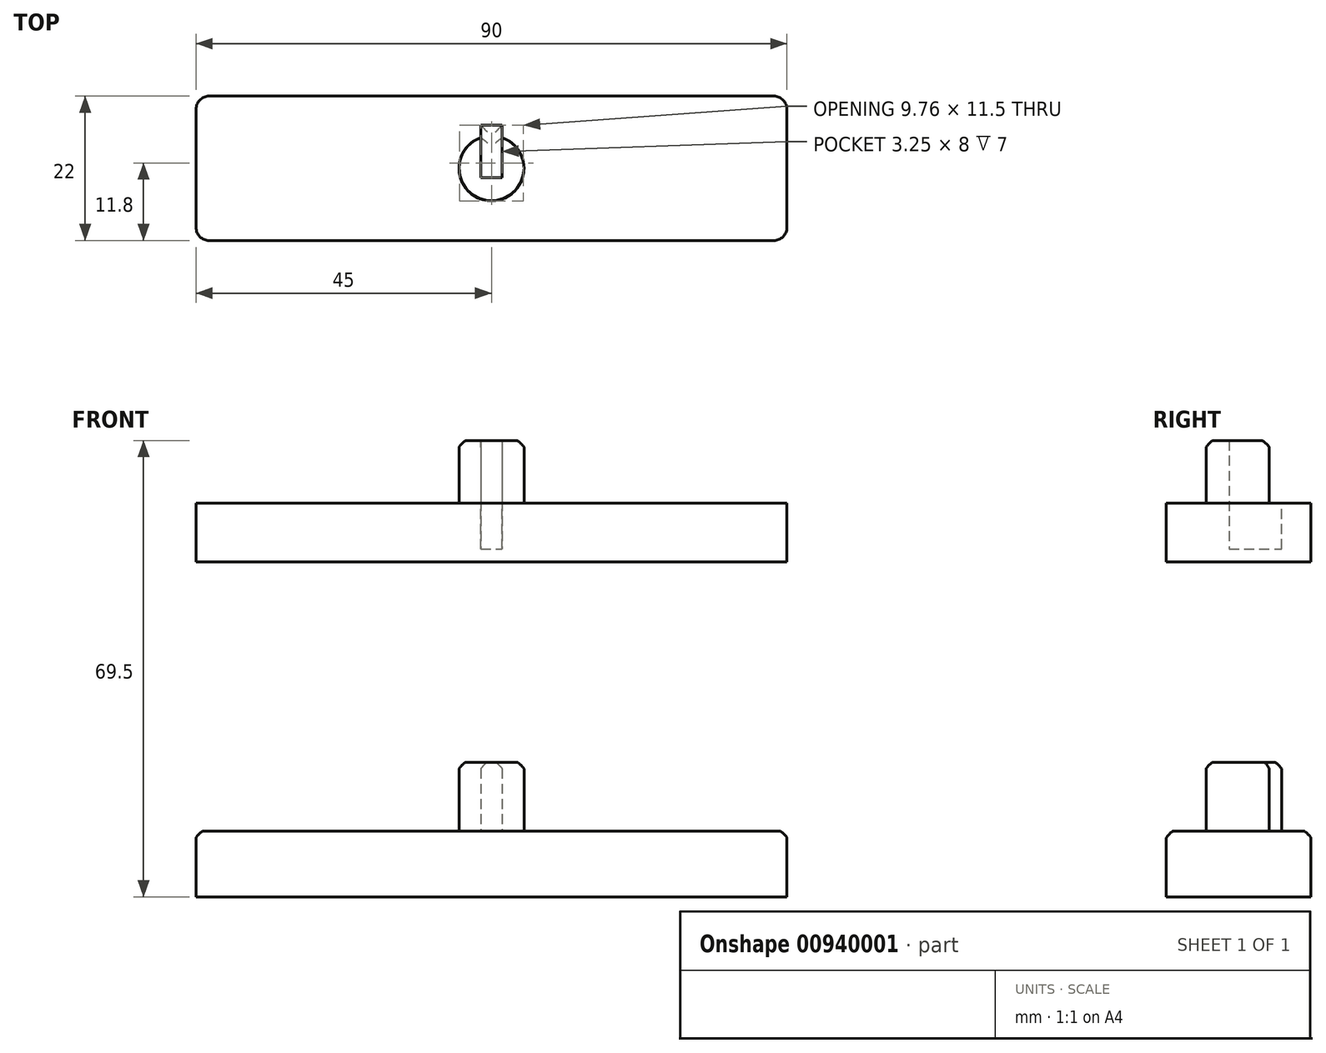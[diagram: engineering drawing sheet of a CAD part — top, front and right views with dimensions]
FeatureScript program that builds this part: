
annotation { "Feature Type Name" : "Feature", "Feature Type Description" : "" }
export const myFeature = defineFeature(function(context is Context, id is Id, definition is map)
    precondition{}
    {
        {
            var Q0;
            Q0=qCreatedBy(makeId("Top.planeOp"),FACE);
            var sketch = newSketch(context, id + "F0", { "sketchPlane" : qUnion([Q0])});
            skLineSegment(sketch, "E0.bottom", {"start": v(-43, 11) * mm, "end": v(43, 11) * mm});
            skLineSegment(sketch, "E0.top", {"start": v(-43, -11) * mm, "end": v(43, -11) * mm});
            skLineSegment(sketch, "E0.left", {"start": v(-45, 9) * mm, "end": v(-45, -9) * mm});
            skLineSegment(sketch, "E0.right", {"start": v(45, 9) * mm, "end": v(45, -9) * mm});
            skPoint(sketch, "E0.middle", {"position": v(0, 0) * mm});
            skArc(sketch, "E1", {"start": v(-1.62, 4.68) * mm, "mid": v(0, -4.95) * mm, "end": v(1.63, 4.68) * mm});
            skLineSegment(sketch, "E2", {"start": v(-1.62, 4.68) * mm, "end": v(-1.62, 6.55) * mm});
            skLineSegment(sketch, "E3", {"start": v(-1.62, 6.55) * mm, "end": v(0, 6.55) * mm});
            skLineSegment(sketch, "E4.MirrorCS", {"start": v(1.62, 4.68) * mm, "end": v(1.62, 6.55) * mm});
            skLineSegment(sketch, "E5.MirrorCS", {"start": v(1.62, 6.55) * mm, "end": v(0, 6.55) * mm});
            skPoint(sketch, "E6.visualSharp", {"position": v(-45, 11) * mm});
            skArc(sketch, "E6.filletArc", {"start": v(-43, 11) * mm, "mid": v(-44.41, 10.41) * mm, "end": v(-45, 9) * mm});
            skPoint(sketch, "E7.visualSharp", {"position": v(-45, -11) * mm});
            skArc(sketch, "E7.filletArc", {"start": v(-45, -9) * mm, "mid": v(-44.41, -10.41) * mm, "end": v(-43, -11) * mm});
            skPoint(sketch, "E8.visualSharp", {"position": v(45, -11) * mm});
            skArc(sketch, "E8.filletArc", {"start": v(43, -11) * mm, "mid": v(44.41, -10.41) * mm, "end": v(45, -9) * mm});
            skPoint(sketch, "E9.visualSharp", {"position": v(45, 11) * mm});
            skArc(sketch, "E9.filletArc", {"start": v(45, 9) * mm, "mid": v(44.41, 10.41) * mm, "end": v(43, 11) * mm});
            skSolve(sketch);
        }
        {
            var Q0;
            Q0=makeQuery(id+"F0.imprint","IMPRINT",FACE,{"disambiguationData":[TD([[makeQuery(id+"F0.imprint","IMPRINT",EDGE,{"derivedFrom":sQuery(id+"F0.wireOp",EDGE,"E1")}),1.0]])]});
            extrude(context, id + "F1", {"entities" : qUnion([Q0]), "depth" : 10.5 * mm, "offsetDistance" : 25 * mm});
        }
        {
            var Q0;
            Q0=makeQuery(id+"F0.imprint","IMPRINT",FACE,{"disambiguationData":[TD([[makeQuery(id+"F0.imprint","IMPRINT",EDGE,{"derivedFrom":sQuery(id+"F0.wireOp",EDGE,"E0.bottom")}),-1.0]])]});
            var Q1;
            Q1=makeQuery(id+"F0.imprint","IMPRINT",FACE,{"disambiguationData":[TD([[makeQuery(id+"F0.imprint","IMPRINT",EDGE,{"derivedFrom":sQuery(id+"F0.wireOp",EDGE,"E1")}),1.0]])]});
            extrude(context, id + "F2", {"entities" : qUnion([Q0, Q1]), "operationType" : NewBodyOperationType.ADD, "oppositeDirection" : true, "depth" : 9 * mm, "offsetDistance" : 25 * mm});
        }
        {
            var Q0;
            Q0=makeQuery(id+"F0.imprint","IMPRINT",FACE,{"disambiguationData":[TD([[makeQuery(id+"F0.imprint","IMPRINT",EDGE,{"derivedFrom":sQuery(id+"F0.wireOp",EDGE,"E0.bottom")}),-1.0]])]});
            var Q1;
            Q1=makeQuery(id+"F0.imprint","IMPRINT",FACE,{"disambiguationData":[TD([[makeQuery(id+"F0.imprint","IMPRINT",EDGE,{"derivedFrom":sQuery(id+"F0.wireOp",EDGE,"E1")}),1.0]])]});
            var Q2;
            Q2=sQuery(id+"F0.wireOp",EDGE,"E0.top");
            var Q3;
            Q3=sQuery(id+"F0.wireOp",EDGE,"E8.filletArc");
            var Q4;
            Q4=sQuery(id+"F0.wireOp",EDGE,"E0.right");
            var Q5;
            Q5=sQuery(id+"F0.wireOp",EDGE,"E9.filletArc");
            var Q6;
            Q6=sQuery(id+"F0.wireOp",EDGE,"E0.bottom");
            var Q7;
            Q7=sQuery(id+"F0.wireOp",EDGE,"E0.left");
            var Q8;
            Q8=sQuery(id+"F0.wireOp",EDGE,"E6.filletArc");
            var Q9;
            Q9=sQuery(id+"F0.wireOp",EDGE,"E7.filletArc");
            extrude(context, id + "F3", {"entities" : qUnion([Q0, Q1]), "operationType" : NewBodyOperationType.ADD, "surfaceEntities" : qUnion([Q2, Q3, Q4, Q5, Q6, Q7, Q8, Q9]), "oppositeDirection" : true, "depth" : 10 * mm, "offsetDistance" : 25 * mm});
        }
        {
            var Q0;
            Q0=makeQuery(id+"F2.opExtrude","CAP_EDGE",EDGE,{"disambiguationData":[OSD([sQuery(id+"F0.wireOp",EDGE,"E0.left")])],"isStart":true});
            var Q1;
            Q1=makeQuery(id+"F1.opExtrude","CAP_FACE",FACE,{"disambiguationData":[OSD([sQuery(id+"F0.wireOp",EDGE,"E1"),sQuery(id+"F0.wireOp",EDGE,"E2"),sQuery(id+"F0.wireOp",EDGE,"E3"),sQuery(id+"F0.wireOp",EDGE,"E4.MirrorCS"),sQuery(id+"F0.wireOp",EDGE,"E5.MirrorCS")])],"isStart":false});
            fillet(context, id + "F4", {"entities" : qUnion([Q0, Q1]), "radius" : 1 * mm, "tangentPropagation" : true, "rho" : .1, "crossSection" : FilletCrossSection.CONIC, "allowEdgeOverflow" : false});
        }
        {
            var Q0;
            Q0=qCreatedBy(makeId("Top.planeOp"),FACE);
            cPlane(context, id + "F5", {"entities" : qUnion([Q0]), "cplaneType" : CPlaneType.OFFSET, "offset" : 50 * mm, "width" : 150 * mm, "height" : 150 * mm});
        }
        {
            var Q0;
            Q0=qCreatedBy(id+"F5.planeOp",FACE);
            var sketch = newSketch(context, id + "F6", { "sketchPlane" : qUnion([Q0])});
            skLineSegment(sketch, "E10.0", {"start": v(-43, 11) * mm, "end": v(43, 11) * mm});
            skArc(sketch, "E10.1.0", {"start": v(-45, -9) * mm, "mid": v(-44.41, -10.41) * mm, "end": v(-43, -11) * mm});
            skLineSegment(sketch, "E10.1.1", {"start": v(-43, -11) * mm, "end": v(43, -11) * mm});
            skArc(sketch, "E10.1.2", {"start": v(43, -11) * mm, "mid": v(44.41, -10.41) * mm, "end": v(45, -9) * mm});
            skLineSegment(sketch, "E10.1.3", {"start": v(45, -9) * mm, "end": v(45, 9) * mm});
            skArc(sketch, "E10.1.4", {"start": v(45, 9) * mm, "mid": v(44.41, 10.41) * mm, "end": v(43, 11) * mm});
            skLineSegment(sketch, "E10.1.5", {"start": v(43, 11) * mm, "end": v(-43, 11) * mm});
            skArc(sketch, "E10.1.6", {"start": v(-43, 11) * mm, "mid": v(-44.41, 10.41) * mm, "end": v(-45, 9) * mm});
            skLineSegment(sketch, "E10.1.7", {"start": v(-45, 9) * mm, "end": v(-45, -9) * mm});
            skLineSegment(sketch, "E10.2.0", {"start": v(1.62, 4.68) * mm, "end": v(1.62, 6.55) * mm});
            skLineSegment(sketch, "E10.2.1", {"start": v(1.62, 6.55) * mm, "end": v(0, 6.55) * mm});
            skLineSegment(sketch, "E10.2.2", {"start": v(0, 6.55) * mm, "end": v(-1.62, 6.55) * mm});
            skLineSegment(sketch, "E10.2.3", {"start": v(-1.62, 6.55) * mm, "end": v(-1.62, 4.68) * mm});
            skArc(sketch, "E10.2.4", {"start": v(-1.63, 4.68) * mm, "mid": v(0, -4.95) * mm, "end": v(1.63, 4.68) * mm});
            skLineSegment(sketch, "E11", {"start": v(1.62, 4.68) * mm, "end": v(1.62, -1.45) * mm});
            skLineSegment(sketch, "E12", {"start": v(1.62, -1.45) * mm, "end": v(-1.62, -1.45) * mm});
            skLineSegment(sketch, "E13", {"start": v(-1.62, -1.45) * mm, "end": v(-1.63, 4.68) * mm});
            skSolve(sketch);
        }
        {
            var Q0;
            Q0=makeQuery(id+"F6.imprint","IMPRINT",FACE,{"disambiguationData":[TD([[makeQuery(id+"F6.imprint","IMPRINT",EDGE,{"derivedFrom":sQuery(id+"F6.wireOp",EDGE,"E10.1.0")}),1.0]])]});
            var Q1;
            Q1=makeQuery(id+"F6.imprint","IMPRINT",FACE,{"disambiguationData":[TD([[makeQuery(id+"F6.imprint","IMPRINT",EDGE,{"derivedFrom":sQuery(id+"F6.wireOp",EDGE,"E10.2.4")}),1.0]])]});
            var Q2;
            Q2=makeQuery(id+"F6.imprint","IMPRINT",FACE,{"disambiguationData":[TD([[makeQuery(id+"F6.imprint","IMPRINT",EDGE,{"derivedFrom":sQuery(id+"F6.wireOp",EDGE,"E10.2.0")}),1.0]])]});
            extrude(context, id + "F7", {"entities" : qUnion([Q0, Q1, Q2]), "oppositeDirection" : true, "depth" : 9 * mm, "offsetDistance" : 25 * mm});
        }
        {
            var Q0;
            Q0=makeQuery(id+"F6.imprint","IMPRINT",FACE,{"disambiguationData":[TD([[makeQuery(id+"F6.imprint","IMPRINT",EDGE,{"derivedFrom":sQuery(id+"F6.wireOp",EDGE,"E10.2.4")}),1.0]])]});
            extrude(context, id + "F8", {"entities" : qUnion([Q0]), "operationType" : NewBodyOperationType.ADD, "depth" : 9.5 * mm, "offsetDistance" : 25 * mm});
        }
        {
            var Q0;
            Q0=makeQuery(id+"F6.imprint","IMPRINT",FACE,{"disambiguationData":[TD([[makeQuery(id+"F6.imprint","IMPRINT",EDGE,{"derivedFrom":sQuery(id+"F6.wireOp",EDGE,"E10.2.0")}),1.0]])]});
            var Q1;
            Q1=makeQuery(id+"F7.opExtrude","CAP_FACE",FACE,{"disambiguationData":[OSD([sQuery(id+"F6.wireOp",EDGE,"E10.1.0"),sQuery(id+"F6.wireOp",EDGE,"E10.1.1"),sQuery(id+"F6.wireOp",EDGE,"E10.1.2"),sQuery(id+"F6.wireOp",EDGE,"E10.1.3"),sQuery(id+"F6.wireOp",EDGE,"E10.1.4"),sQuery(id+"F6.wireOp",EDGE,"E10.1.5"),sQuery(id+"F6.wireOp",EDGE,"E10.1.6"),sQuery(id+"F6.wireOp",EDGE,"E10.1.7")])],"isStart":false});
            extrude(context, id + "F9", {"entities" : qUnion([Q0]), "operationType" : NewBodyOperationType.REMOVE, "endBound" : BoundingType.UP_TO_SURFACE, "oppositeDirection" : true, "depth" : 5 * mm, "endBoundEntityFace" : qUnion([Q1]), "hasOffset" : true, "offsetDistance" : 2 * mm});
        }
        {
            var Q0;
            Q0=makeQuery(id+"F7.opExtrude","CAP_EDGE",EDGE,{"disambiguationData":[OSD([sQuery(id+"F6.wireOp",EDGE,"E10.1.5")])],"isStart":true});
            var Q1;
            Q1=makeQuery(id+"F8.opExtrude","CAP_EDGE",EDGE,{"disambiguationData":[OSD([sQuery(id+"F6.wireOp",EDGE,"E10.2.4")])],"isStart":false});
            fillet(context, id + "F10", {"entities" : qUnion([Q0, Q1]), "radius" : 1 * mm, "tangentPropagation" : true, "rho" : .1, "crossSection" : FilletCrossSection.CONIC, "allowEdgeOverflow" : false});
        }
    });
